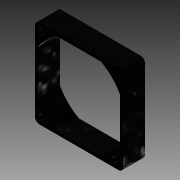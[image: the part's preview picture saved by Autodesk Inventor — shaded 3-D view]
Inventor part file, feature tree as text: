
AUTODESK INVENTOR PART (.ipt)
format: ipt  version: 2015 (Build 190159000, 159)  size: 125,952 bytes
history: native  units: in
note: dims shown in document units (in); Inventor stores cm internally (conversion verified against a paired STEP export)
features: extrude x3, sketch x3, projected_geometry x2, fillet x1
ambient origin geometry x8: Origin, YZ Plane, XZ Plane, XY Plane, X Axis, Y Axis, Z Axis, Center Point
bodies: Solid1 (feature_tree)
feature tree (9):
  extrude  "Extrusion1"  Depth=2.3622in
  extrude  "Extrusion2"  Depth=0.5906in
  extrude  "Extrusion3"  Depth=0.125in
  fillet  "Fillet2"  Radius=0.1693in
  sketch  "Sketch1"  dims[d0=2.3622in d1=2.3622in]
  sketch  "Sketch2"  dims[d2=0.5906in d3=0.0in d5=0.1693in]
  projected_geometry  "Projected Loop1"
  sketch  "Sketch3"  dims[d6=0.1693in d7=0.1693in d8=0.1693in d9=1.9685in d10=1.9685in d11=0.1969in d12=0.1969in d13=0.5906in d14=0.0in d16=2.3622in d17=1.1811in d18=1.1811in d19=2.5in d20=0.0787in d21=1.5748in d23=360.0deg d25=0.5906in d26=0.0in d27=0.125in]
  projected_geometry  "Projected Loop2"
